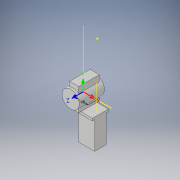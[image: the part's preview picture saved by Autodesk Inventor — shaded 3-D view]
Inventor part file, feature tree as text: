
AUTODESK INVENTOR PART (.ipt)
format: ipt  version: 2019 (Build 230136000, 136)  size: 146,432 bytes
history: native  units: in
note: dims shown in document units (in); Inventor stores cm internally (conversion verified against a paired STEP export)
features: other x10, sketch x5, extrude x4, plane x2
ambient origin geometry x4: Origin, YZ Plane, XZ Plane, XY Plane
bodies: Solid1 (feature_tree)
feature tree (21):
  extrude  "Extrusion1"  Depth=3.4646in TaperAngle=0.0deg
  other  "Work Point1"
  other  "Work Point2"
  sketch  "Sketch2"  dims[d3=0.0in d4=0.0in d5=0.0in d6=0.0in d7=0.0in d8=0.0in d11=1.8898in]
  other  "Work Point 3"
  plane  "Work Plane1"
  extrude  "Extrusion2"  Depth=1.8898in
  extrude  "Extrusion3"  Depth=0.4724in
  extrude  "Extrusion4"  Depth=2.2047in
  sketch  "Sketch1"  dims[d0=2.3622in d1=3.4646in d2=0.0in]
  sketch  "Sketch3"  dims[d12=-1.4173in d13=0.4724in]
  sketch  "Sketch4"  dims[d14=2.2047in d15=2.3622in]
  sketch  "Sketch5"  dims[d16=0.315in d17=0.0in d18=1.2598in d19=0.315in d20=3.1496in d21=0.0in d22=1.5748in d23=2.2047in d24=3.7795in d25=0.0in d26=7.2441in]
  plane  "Work Plane2"
  other  "UCS3: YZ Plane"
  other  "UCS3: XZ Plane"
  other  "UCS3: XY Plane"
  other  "UCS3: X Axis"
  other  "UCS3: Y Axis"
  other  "UCS3: Z Axis"
  other  "UCS3: Center Point"
